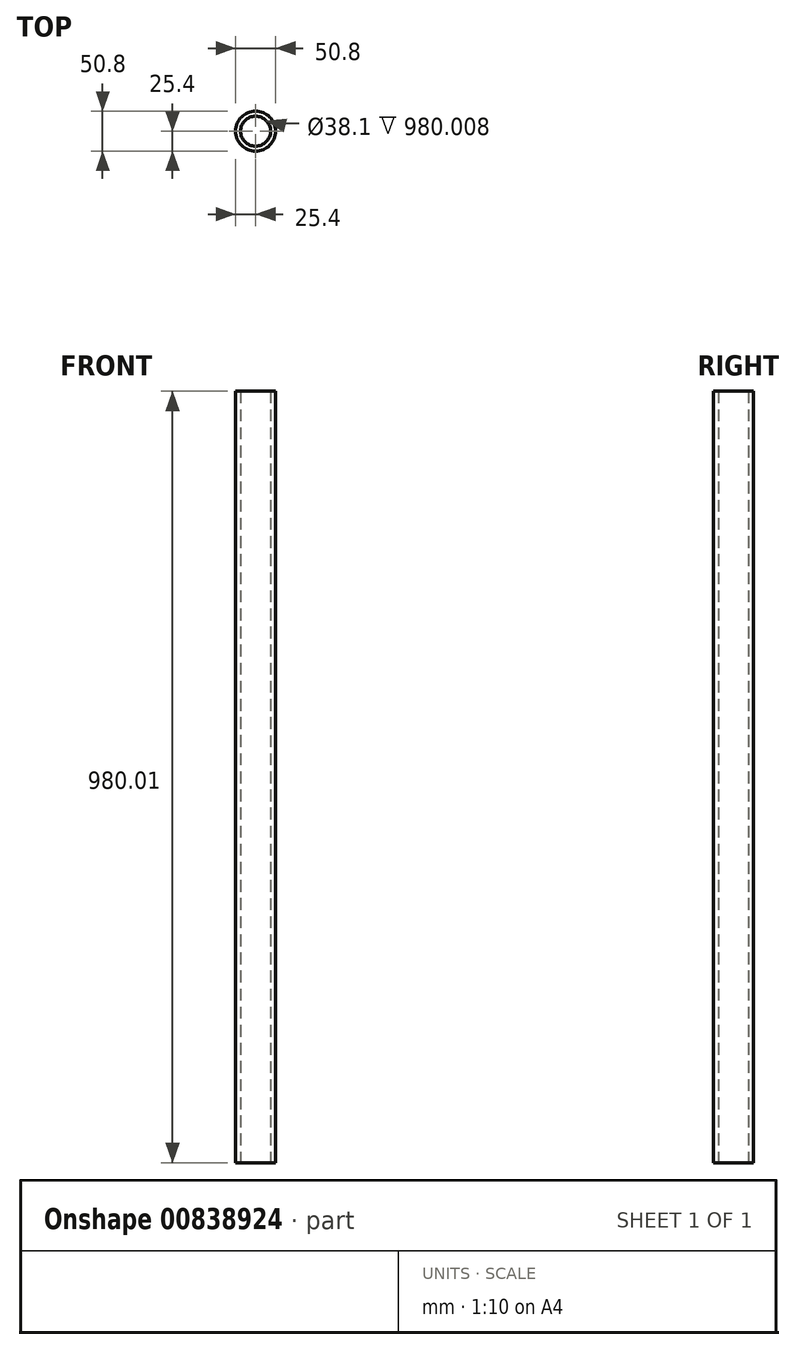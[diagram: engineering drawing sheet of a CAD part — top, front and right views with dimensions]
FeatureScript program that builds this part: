
annotation { "Feature Type Name" : "Feature", "Feature Type Description" : "" }
export const myFeature = defineFeature(function(context is Context, id is Id, definition is map)
    precondition{}
    {
        {
            var Q0;
            Q0=qCreatedBy(makeId("Top.planeOp"),FACE);
            var sketch = newSketch(context, id + "F0", { "sketchPlane" : qUnion([Q0])});
            skCircle(sketch, "E0", {"center": v(0, 0) * mm, "radius": 25.4 * mm});
            skCircle(sketch, "E1", {"center": v(0, 0) * mm, "radius": 19.05 * mm});
            skSolve(sketch);
        }
        {
            var Q0;
            Q0 = qSketchRegion(id + "F0", true);
            extrude(context, id + "F1", {"entities" : qUnion([Q0]), "depth" : 980 * mm, "offsetDistance" : 25.4 * mm});
        }
    });
